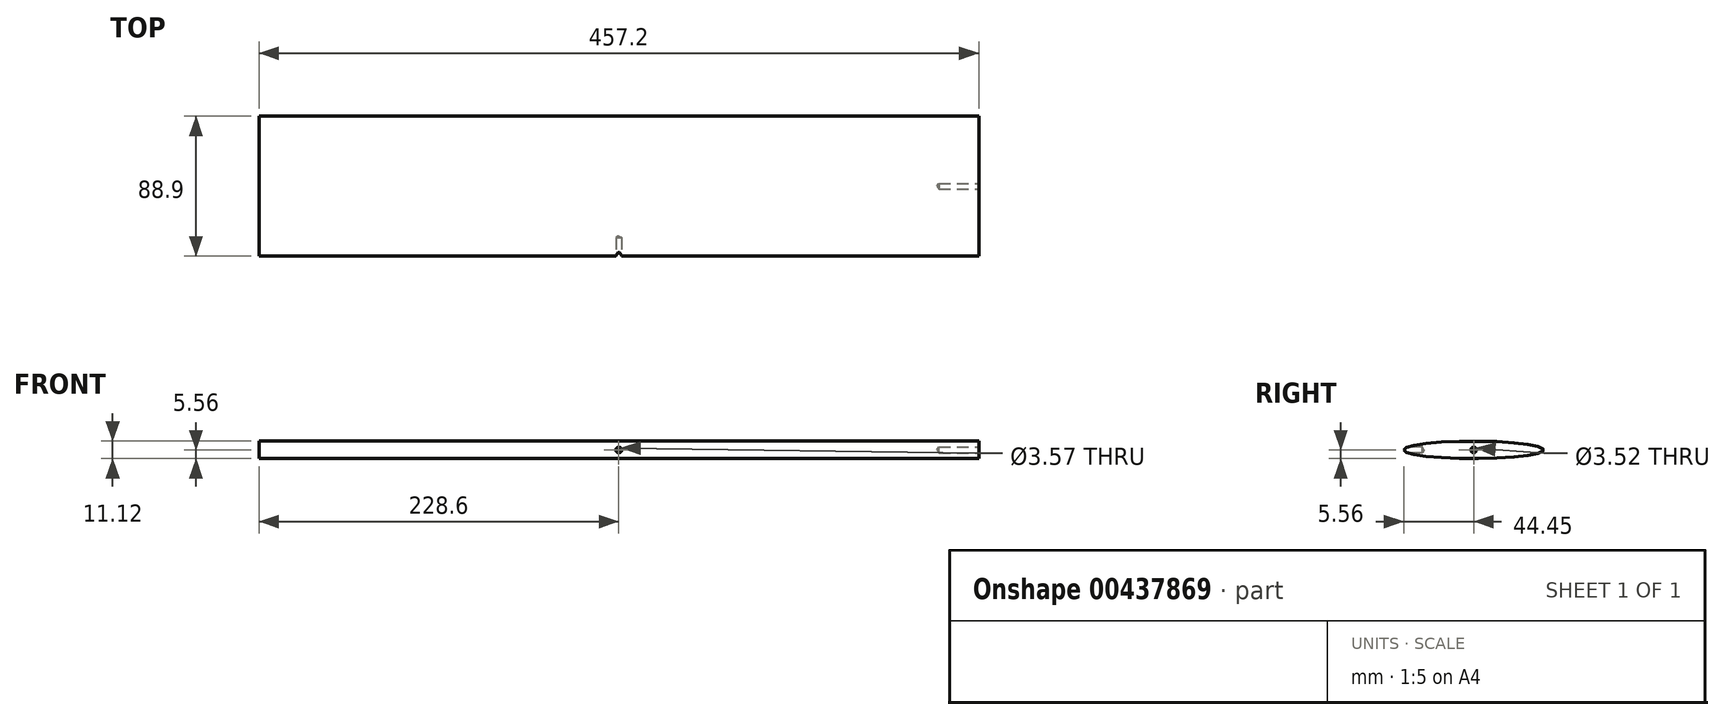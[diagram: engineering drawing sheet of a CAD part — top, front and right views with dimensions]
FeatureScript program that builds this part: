
annotation { "Feature Type Name" : "Feature", "Feature Type Description" : "" }
export const myFeature = defineFeature(function(context is Context, id is Id, definition is map)
    precondition{}
    {
        {
            var Q0;
            Q0=qCreatedBy(makeId("Right.planeOp"),FACE);
            var sketch = newSketch(context, id + "F0", { "sketchPlane" : qUnion([Q0])});
            skEllipse(sketch, "E0", {"center": v(0, 0) * mm, "majorRadius": 44.45 * mm, "minorRadius": 5.56 * mm, "majorAxis": v(-1, 0)});
            skSolve(sketch);
        }
        {
            var Q0;
            Q0=makeQuery(id+"F0.imprint","IMPRINT",FACE,{"disambiguationData":[TD([[makeQuery(id+"F0.imprint","IMPRINT",EDGE,{"derivedFrom":sQuery(id+"F0.wireOp",EDGE,"E0")}),1.0]])]});
            extrude(context, id + "F1", {"entities" : qUnion([Q0]), "depth" : 457.2 * mm, "symmetric" : true});
        }
        {
            var Q0;
            Q0=makeQuery(id+"F1.opExtrude","CAP_FACE",FACE,{"disambiguationData":[OSD([sQuery(id+"F0.wireOp",EDGE,"E0")])],"isStart":false});
            var sketch = newSketch(context, id + "F2", { "sketchPlane" : qUnion([Q0])});
            skPoint(sketch, "E1", {"position": v(0, 0) * mm});
            skSolve(sketch);
        }
        {
            var Q0;
            Q0=sQuery(id+"F2.wireOp",VERTEX,"E1");
            var Q1;
            Q1=makeQuery(id+"F1.opExtrude","SWEPT_BODY",BODY,{"disambiguationData":[OSD([sQuery(id+"F0.wireOp",EDGE,"E0")])]});
            hole(context, id + "F3", {"style" : HoleStyle.SIMPLE, "endStyle" : HoleEndStyle.BLIND, "holeDiameter" : 3.52 * mm, "holeDepth" : 25.4 * mm, "isTappedThrough" : true, "tappedDepth" : 12.7 * mm, "tapClearance" : 3, "locations" : qUnion([Q0]), "scope" : qUnion([Q1])});
        }
        {
            var Q0;
            Q0=qCreatedBy(makeId("Front.planeOp"),FACE);
            cPlane(context, id + "F4", {"entities" : qUnion([Q0]), "cplaneType" : CPlaneType.OFFSET, "offset" : 44.45 * mm, "width" : 152.4 * mm, "height" : 152.4 * mm});
        }
        {
            var Q0;
            Q0=qCreatedBy(id+"F4.planeOp",FACE);
            var sketch = newSketch(context, id + "F5", { "sketchPlane" : qUnion([Q0])});
            skPoint(sketch, "E2", {"position": v(0, 0) * mm});
            skSolve(sketch);
        }
        {
            var Q0;
            Q0=sQuery(id+"F5.wireOp",VERTEX,"E2");
            var Q1;
            Q1=makeQuery(id+"F1.opExtrude","SWEPT_BODY",BODY,{"disambiguationData":[OSD([sQuery(id+"F0.wireOp",EDGE,"E0")])]});
            hole(context, id + "F6", {"style" : HoleStyle.SIMPLE, "endStyle" : HoleEndStyle.BLIND, "holeDiameter" : 3.57 * mm, "holeDepth" : 9.52 * mm, "isTappedThrough" : true, "tappedDepth" : 12.7 * mm, "tapClearance" : 3, "locations" : qUnion([Q0]), "scope" : qUnion([Q1])});
        }
    });
